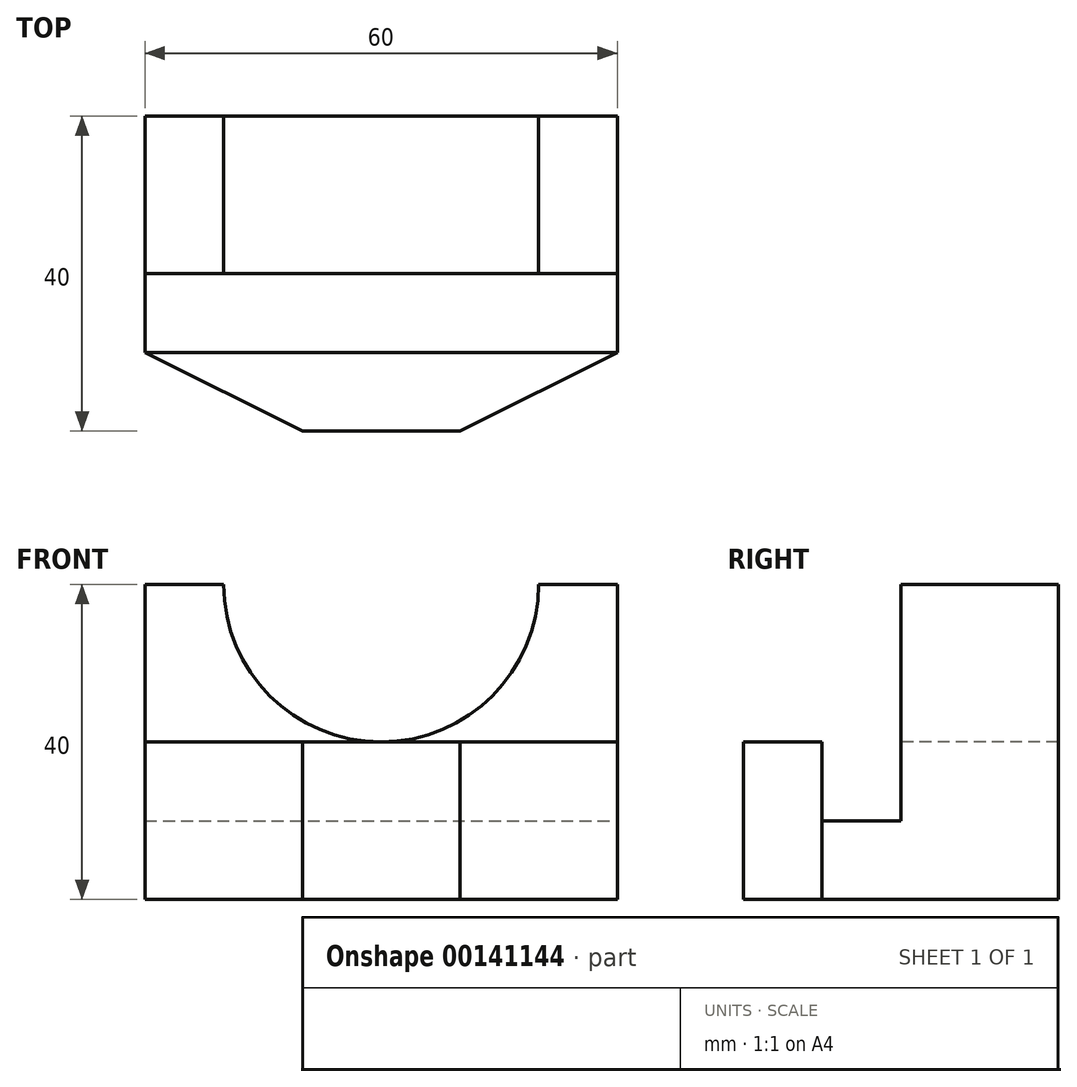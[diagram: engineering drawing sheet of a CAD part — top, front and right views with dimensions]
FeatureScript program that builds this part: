
annotation { "Feature Type Name" : "Feature", "Feature Type Description" : "" }
export const myFeature = defineFeature(function(context is Context, id is Id, definition is map)
    precondition{}
    {
        {
            var Q0;
            Q0=qCreatedBy(makeId("Front.planeOp"),FACE);
            var sketch = newSketch(context, id + "F0", { "sketchPlane" : qUnion([Q0])});
            skLineSegment(sketch, "E0.bottom", {"start": v(-30, 0) * mm, "end": v(-20, 0) * mm});
            skLineSegment(sketch, "E0.top", {"start": v(-30, -40) * mm, "end": v(30, -40) * mm});
            skLineSegment(sketch, "E0.left", {"start": v(-30, 0) * mm, "end": v(-30, -40) * mm});
            skLineSegment(sketch, "E0.right", {"start": v(30, 0) * mm, "end": v(30, -40) * mm});
            skArc(sketch, "E1", {"start": v(-20, 0) * mm, "mid": v(0, -20) * mm, "end": v(20, 0) * mm});
            skLineSegment(sketch, "E2.trimOffspring", {"start": v(20, 0) * mm, "end": v(30, 0) * mm});
            skSolve(sketch);
        }
        {
            var Q0;
            Q0=makeQuery(id+"F0.imprint","IMPRINT",FACE,{"disambiguationData":[TD([[makeQuery(id+"F0.imprint","IMPRINT",EDGE,{"derivedFrom":sQuery(id+"F0.wireOp",EDGE,"E0.bottom")}),-1.0]])]});
            extrude(context, id + "F1", {"entities" : qUnion([Q0]), "endBound" : BoundingType.SYMMETRIC, "oppositeDirection" : true, "depth" : 40 * mm});
        }
        {
            var Q0;
            Q0=qCreatedBy(makeId("Right.planeOp"),FACE);
            var sketch = newSketch(context, id + "F2", { "sketchPlane" : qUnion([Q0])});
            skLineSegment(sketch, "E3", {"start": v(0, 0) * mm, "end": v(0, -30) * mm});
            skLineSegment(sketch, "E4", {"start": v(0, -30) * mm, "end": v(-10, -30) * mm});
            skLineSegment(sketch, "E5", {"start": v(-10, -30) * mm, "end": v(-10, -20) * mm});
            skLineSegment(sketch, "E6", {"start": v(-10, -20) * mm, "end": v(-20, -20) * mm});
            skLineSegment(sketch, "E7", {"start": v(-20, -20) * mm, "end": v(-20, 0) * mm});
            skLineSegment(sketch, "E8", {"start": v(-20, 0) * mm, "end": v(0, 0) * mm});
            skSolve(sketch);
        }
        {
            var Q0;
            Q0 = qSketchRegion(id + "F2", true);
            extrude(context, id + "F3", {"entities" : qUnion([Q0]), "operationType" : NewBodyOperationType.REMOVE, "endBound" : BoundingType.SYMMETRIC, "oppositeDirection" : true, "depth" : 60 * mm});
        }
        {
            var Q0;
            Q0=qCreatedBy(makeId("Top.planeOp"),FACE);
            var sketch = newSketch(context, id + "F4", { "sketchPlane" : qUnion([Q0])});
            skLineSegment(sketch, "E9", {"start": v(-30, -10) * mm, "end": v(-10, -20) * mm});
            skLineSegment(sketch, "E10", {"start": v(-10, -20) * mm, "end": v(-30, -20) * mm});
            skLineSegment(sketch, "E11", {"start": v(-30, -20) * mm, "end": v(-30, -10) * mm});
            skLineSegment(sketch, "E12", {"start": v(30, -10) * mm, "end": v(30, -20) * mm});
            skLineSegment(sketch, "E13", {"start": v(30, -20) * mm, "end": v(10, -20) * mm});
            skLineSegment(sketch, "E14", {"start": v(10, -20) * mm, "end": v(30, -10) * mm});
            skSolve(sketch);
        }
        {
            var Q0;
            Q0 = qSketchRegion(id + "F4", true);
            extrude(context, id + "F5", {"entities" : qUnion([Q0]), "operationType" : NewBodyOperationType.REMOVE, "endBound" : BoundingType.THROUGH_ALL, "oppositeDirection" : true, "depth" : 50.9 * mm});
        }
    });
